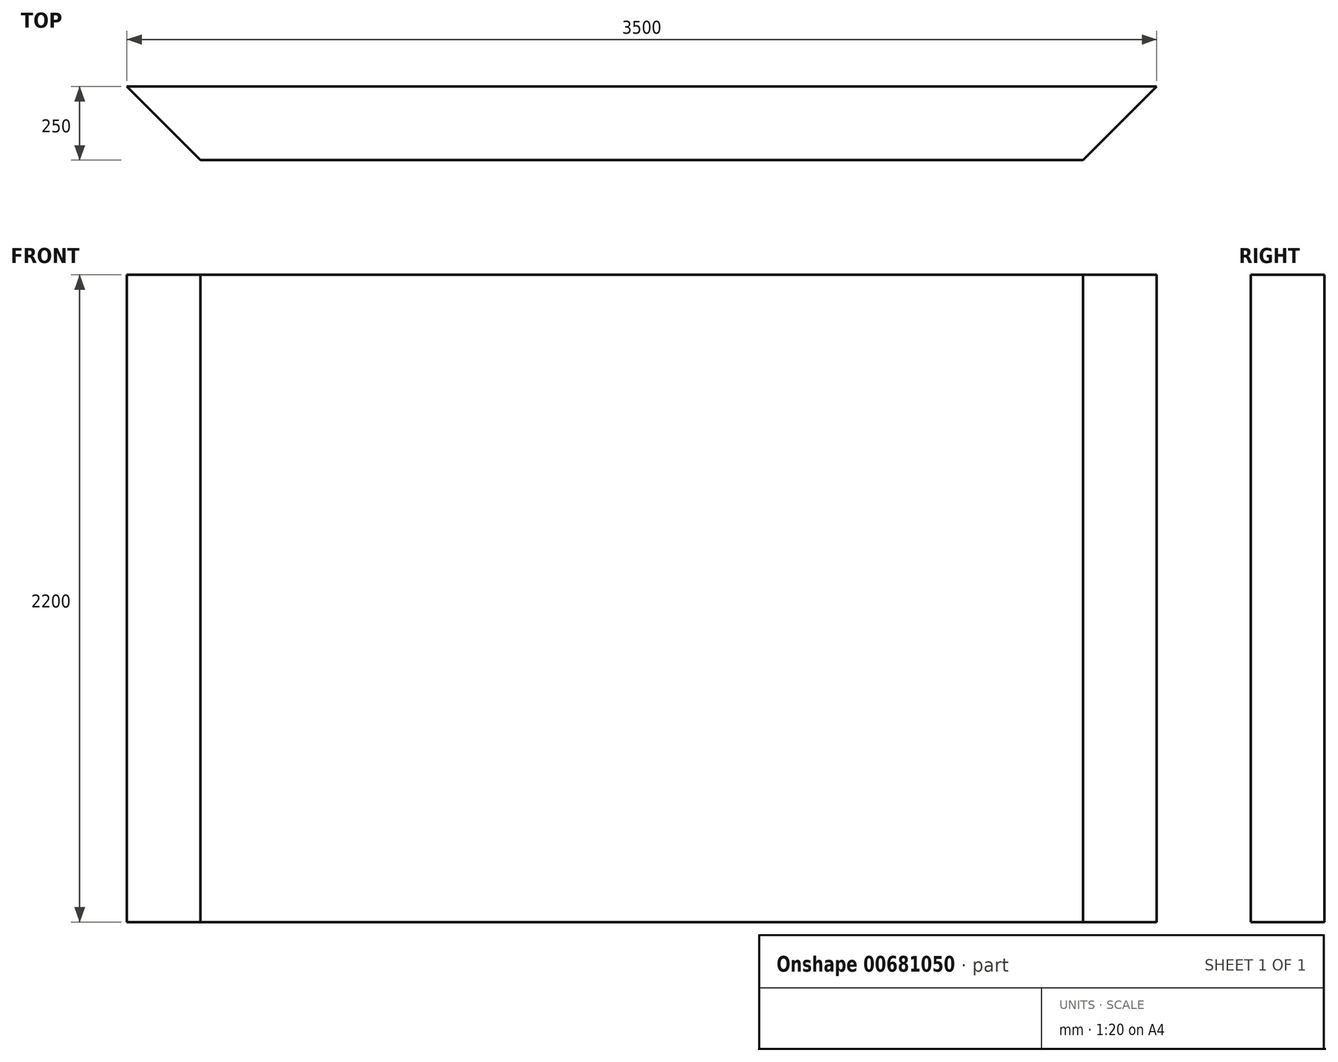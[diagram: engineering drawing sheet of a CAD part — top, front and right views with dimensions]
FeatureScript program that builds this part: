
annotation { "Feature Type Name" : "Feature", "Feature Type Description" : "" }
export const myFeature = defineFeature(function(context is Context, id is Id, definition is map)
    precondition{}
    {
        {
            var Q0;
            Q0=qCreatedBy(makeId("Front.planeOp"),FACE);
            var sketch = newSketch(context, id + "F0", { "sketchPlane" : qUnion([Q0])});
            skLineSegment(sketch, "E0.bottom", {"start": v(0, 0) * mm, "end": v(3500, 0) * mm});
            skLineSegment(sketch, "E0.top", {"start": v(0, 2200) * mm, "end": v(3500, 2200) * mm});
            skLineSegment(sketch, "E0.left", {"start": v(0, 0) * mm, "end": v(0, 2200) * mm});
            skLineSegment(sketch, "E0.right", {"start": v(3500, 0) * mm, "end": v(3500, 2200) * mm});
            skSolve(sketch);
        }
        {
            var Q0;
            Q0=qSketchRegion(id+"F0",true);
            extrude(context, id + "F1", {"entities" : qUnion([Q0]), "depth" : 250 * mm, "offsetDistance" : 25 * mm});
        }
        {
            var Q0;
            Q0=makeQuery(id+"F1.opExtrude","SWEPT_FACE",FACE,{"disambiguationData":[OSD([sQuery(id+"F0.wireOp",EDGE,"E0.top")])]});
            var sketch = newSketch(context, id + "F2", { "sketchPlane" : qUnion([Q0])});
            skLineSegment(sketch, "E1", {"start": v(0, 0) * mm, "end": v(250, -250) * mm});
            skLineSegment(sketch, "E2", {"start": v(250, -250) * mm, "end": v(0, -250) * mm});
            skLineSegment(sketch, "E3", {"start": v(0, -250) * mm, "end": v(0, 0) * mm});
            skLineSegment(sketch, "E4", {"start": v(3500, -250) * mm, "end": v(3250, -250) * mm});
            skLineSegment(sketch, "E5", {"start": v(3250, -250) * mm, "end": v(3500, 0) * mm});
            skLineSegment(sketch, "E6", {"start": v(3500, 0) * mm, "end": v(3500, -250) * mm});
            skLineSegment(sketch, "E7", {"start": v(1750, -250) * mm, "end": v(1750, 0) * mm, "construction": true});
            skSolve(sketch);
        }
        {
            var Q0;
            Q0=qSketchRegion(id+"F2",true);
            extrude(context, id + "F3", {"entities" : qUnion([Q0]), "operationType" : NewBodyOperationType.REMOVE, "endBound" : BoundingType.THROUGH_ALL, "oppositeDirection" : true, "depth" : 25 * mm, "offsetDistance" : 25 * mm});
        }
    });
